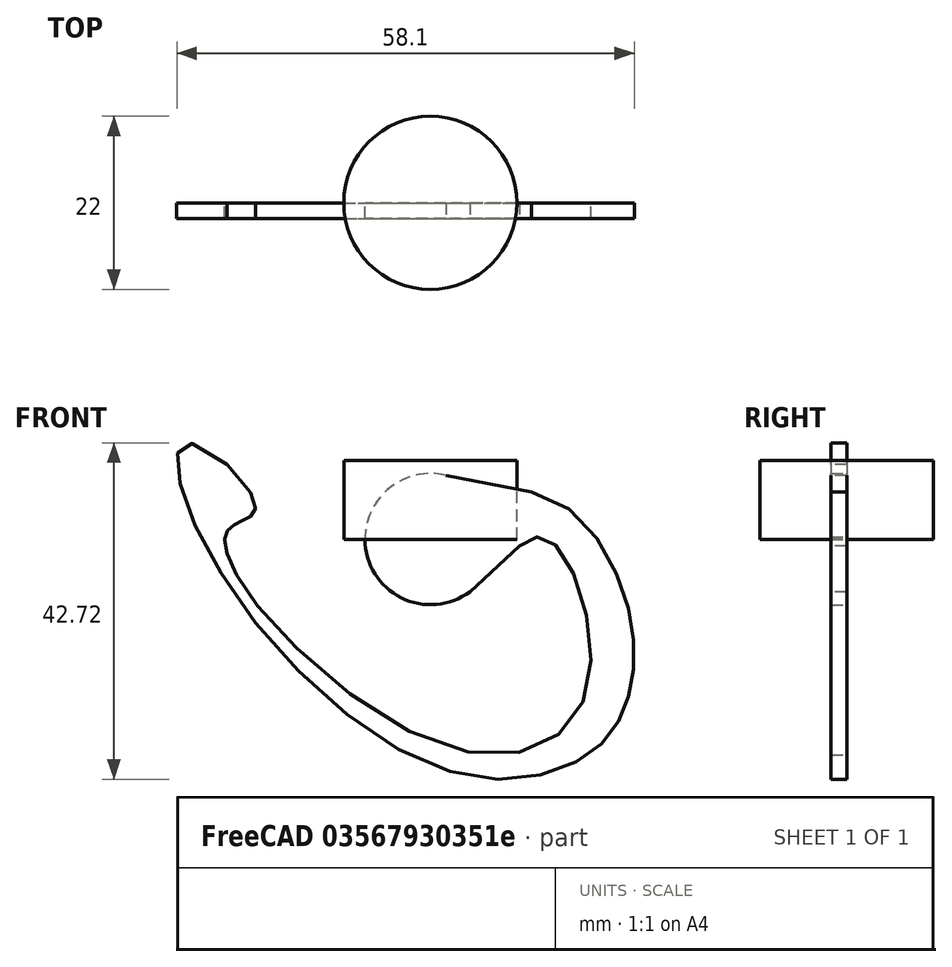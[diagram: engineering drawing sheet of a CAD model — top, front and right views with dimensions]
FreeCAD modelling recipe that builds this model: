
FCSTD DOCUMENT  (FreeCAD 1.0R39319 (Git))
Label: inEar Headset Fix
License: All rights reserved
LicenseURL: https://en.wikipedia.org/wiki/All_rights_reserved
objects: PartDesign::Body×2, Mesh::Feature×1, Sketcher::SketchObject×1, PartDesign::Pad×1, PartDesign::AdditiveCylinder×1
note: 10 computed .brp shape members not serialized (recipe doc carries the construction recipe); baked Part::Feature solids carry a one-line shape summary decoded from their .brp

FEATURE [Mesh::Feature] Ear_Hook_V3_v4
  Placement = pos=(0,3.52,0) rot=(0,0,1;0rad)
FEATURE [Sketcher::SketchObject] Sketch
  ArcFitTolerance = 1e-06
  AttachmentSupport = -> [XZ_Plane]
  FullyConstrained = true
  MakeInternals = false
  MapMode = 5
  Placement = pos=(0,0,0) rot=(1,0,0;1.5708rad)
  sketch-geometry (49):
    g0-g9: Circle [constr] x10 (B-spline internal-alignment scaffolding for g10; pole/knot coordinates omitted)
    g10: BSplineCurve PolesCount=10 KnotsCount=8 Degree=3 IsPeriodic=0
    g11-g18: GeomPoint [constr] x8 (B-spline internal-alignment scaffolding for g10; pole/knot coordinates omitted)
    g19-g32: Circle [constr] x14 (B-spline internal-alignment scaffolding for g33; pole/knot coordinates omitted)
    g33: BSplineCurve PolesCount=14 KnotsCount=12 Degree=3 IsPeriodic=0
    g34-g45: GeomPoint [constr] x12 (B-spline internal-alignment scaffolding for g33; pole/knot coordinates omitted)
    g46: LineSegment StartX=12.85 StartY=6 StartZ=0 EndX=1.97 EndY=8.13 EndZ=0
    g47: LineSegment StartX=11.3 StartY=-0.85 StartZ=0 EndX=5 EndY=-6.65 EndZ=0
    g48: ArcOfCircle CenterX=0.0240522 CenterY=0.0304823 CenterZ=0 NormalX=0 NormalY=0 NormalZ=1 AngleXU=0 Radius=8.33 StartAngle=1.33501 EndAngle=5.35259
  constraints (64):
    c: Weight(g0) = 1
    c: Equal(g0, g1-g9) x9
    c: InternalAlignment(g0-g9 -> g10) x10
    c: InternalAlignment(g11-g18 -> g10) x8
    c: Distance(g10,g-2) = 25.85
    c: Distance(g10,g-1) = 9.5
    c: Distance(g12,g-1) = 5.65
    c: Distance(g12,g-2) = 31.4
    c: Distance(g13,g-1) = 14.15
    c: Distance(g13,g-2) = 19.2
    c: Distance(g14,g-2) = 1.55
    c: Distance(g14,g-1) = 29.2
    c: Distance(g15,g-2) = 19
    c: Distance(g15,g-1) = 28
    c: Distance(g16,g-1) = 18.5
    c: Distance(g16,g-2) = 25.5
    c: Distance(g17,g-2) = 24.15
    c: DistanceY(g17,g-1) = 5.7
    c: Distance(g10,g-2) = 12.85
    c: Distance(g10,g-1) = 6
    c: Distance(g1,g-2) = 32.35
    c: Distance(g1,g-1) = 15.1
    c: Distance(g8,g-2) = 18.81
    c: Distance(g8,g-1) = 4.9
    c: Weight(g19) = 1
    c: Equal(g19, g20-g32) x13
    c: InternalAlignment(g19-g32 -> g33) x14
    c: InternalAlignment(g34-g45 -> g33) x12
    c: Coincident(g19,g10)
    c: Distance(g35,g-2) = 22.25
    c: DistanceY(g-1,g35) = 3.8
    c: DistanceX(g20,g-1) = 22.6
    c: DistanceY(g-1,g36) = 2.3
    c: DistanceX(g36,g-1) = 24.1
    c: DistanceX(g37,g-1) = 25.9
    c: DistanceY(g-1,g37) = 0.85
    c: DistanceX(g38,g-1) = 25.55
    c: DistanceY(g38,g-1) = 2.65
    c: DistanceY(g39,g-1) = 10.7
    c: DistanceX(g39,g-1) = 20
    c: DistanceY(g40,g-1) = 22.5
    c: DistanceX(g40,g-1) = 6.12
    c: DistanceY(g41,g-1) = 27.35
    c: DistanceX(g-1,g41) = 9.05
    c: DistanceX(g-1,g42) = 18.75
    c: DistanceY(g42,g-1) = 21.9
    c: DistanceX(g-1,g43) = 20.05
    c: DistanceY(g43,g-1) = 10.7
    c: DistanceX(g-1,g44) = 16.13
    c: DistanceY(g44,g-1) = 0.95
    c: DistanceX(g-1,g33) = 11.3
    c: DistanceY(g33,g-1) = 0.85
    c: DistanceX(g-1,g30) = 16.2
    c: DistanceY(g-1,g30) = 1.15
    c: DistanceY(g-1,g21) = 3.12
    c: Coincident(g46,g10)
    c: Coincident(g47,g33)
    c: Coincident(g48,g47)
    c: Coincident(g48,g46)
    c: Distance(g46,g-2) = 1.97
    c: Distance(g46,g-1) = 8.13
    c: Distance(g47,g-2) = 5
    c: Distance(g47,g-1) = 6.65
    c: Radius(g48) = 8.33
FEATURE [PartDesign::Pad] Pad
  Direction = (0,-1,2e-16)
  Length = 2
  Length2 = 10
  Placement = pos=(0,0,0) rot=(1,0,0;1.5708rad)
  Profile = -> Sketch
  ReferenceAxis = -> Sketch [N_Axis]
  Refine = true
  Suppressed = false
  Type = 0
FEATURE [PartDesign::Body] Body  label="ear shape"
  AllowCompound = false
  Group = -> [Sketch,Pad]
  Origin = -> Origin
  Tip = -> Pad
FEATURE [PartDesign::AdditiveCylinder] Cylinder
  Angle = 360
  AttacherType = Attacher::AttachEngine3D
  AttachmentOffset = pos=(2,0,0) rot=(0,-1,0;0.785398rad)
  AttachmentSupport = -> [XY_Plane001]
  FirstAngle = 0
  Height = 10
  MapMode = 5
  Placement = pos=(2,0,0) rot=(0,-1,0;0.785398rad)
  Radius = 11
  Refine = true
  SecondAngle = 0
  Suppressed = false
FEATURE [PartDesign::Body] Body001  label="left"
  AllowCompound = false
  Group = -> [Cylinder]
  Origin = -> Origin001
  Tip = -> Cylinder
